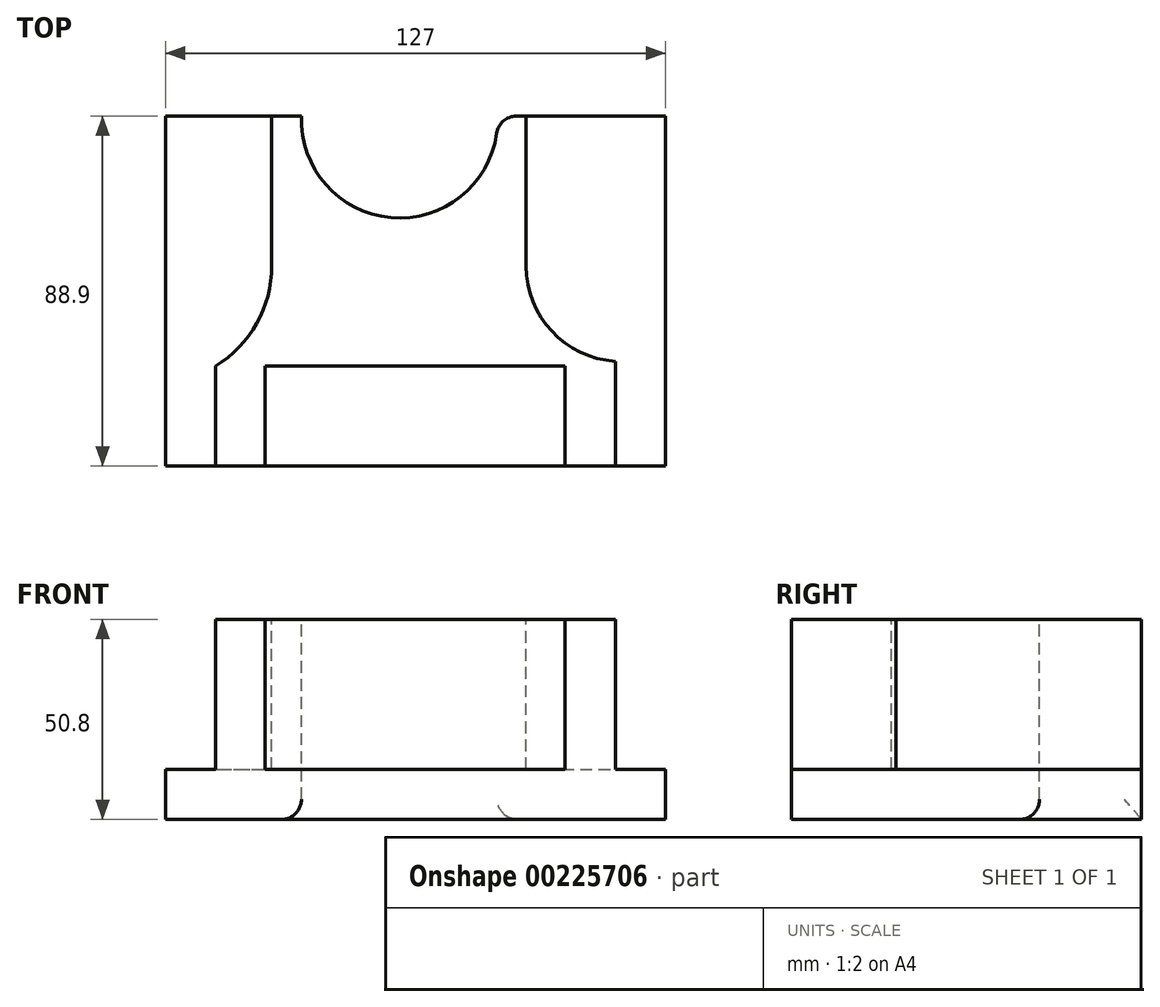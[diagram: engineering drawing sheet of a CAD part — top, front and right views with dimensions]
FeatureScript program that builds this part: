
annotation { "Feature Type Name" : "Feature", "Feature Type Description" : "" }
export const myFeature = defineFeature(function(context is Context, id is Id, definition is map)
    precondition{}
    {
        {
            var Q0;
            Q0=qCreatedBy(makeId("Top.planeOp"),FACE);
            var sketch = newSketch(context, id + "F0", { "sketchPlane" : qUnion([Q0])});
            skLineSegment(sketch, "E0.bottom", {"start": v(-62.55, 34.48) * mm, "end": v(64.45, 34.48) * mm});
            skLineSegment(sketch, "E0.top", {"start": v(-62.55, -54.42) * mm, "end": v(64.45, -54.42) * mm});
            skLineSegment(sketch, "E0.left", {"start": v(-62.55, 34.48) * mm, "end": v(-62.55, -54.42) * mm});
            skLineSegment(sketch, "E0.right", {"start": v(64.45, 34.48) * mm, "end": v(64.45, -54.42) * mm});
            skSolve(sketch);
        }
        {
            var Q0;
            Q0=makeQuery(id+"F0.imprint","IMPRINT",FACE,{"disambiguationData":[TD([[makeQuery(id+"F0.imprint","IMPRINT",EDGE,{"derivedFrom":sQuery(id+"F0.wireOp",EDGE,"E0.bottom")}),-1.0]])]});
            extrude(context, id + "F1", {"entities" : qUnion([Q0]), "depth" : 50.8 * mm});
        }
        {
            var Q0;
            Q0=makeQuery(id+"F1.opExtrude","CAP_FACE",FACE,{"disambiguationData":[OSD([sQuery(id+"F0.wireOp",EDGE,"E0.bottom"),sQuery(id+"F0.wireOp",EDGE,"E0.top"),sQuery(id+"F0.wireOp",EDGE,"E0.left"),sQuery(id+"F0.wireOp",EDGE,"E0.right")])],"isStart":false});
            var sketch = newSketch(context, id + "F2", { "sketchPlane" : qUnion([Q0])});
            skArc(sketch, "E1", {"start": v(-28.02, 34.48) * mm, "mid": v(-3.13, 8.61) * mm, "end": v(21.76, 34.48) * mm});
            skSolve(sketch);
        }
        {
            var Q0;
            {var subQ0=sQuery(id+"F2.wireOp",EDGE,"E1");Q0=makeQuery(id+"F2.imprint","IMPRINT",FACE,{"disambiguationData":[TD([[makeQuery(id+"F2.imprint","IMPRINT",EDGE,{"derivedFrom":subQ0}),1.0]])]});}
            extrude(context, id + "F3", {"entities" : qUnion([Q0]), "operationType" : NewBodyOperationType.REMOVE, "oppositeDirection" : true, "depth" : 76.2 * mm});
        }
        {
            var Q0;
            Q0=makeQuery(id+"F1.opExtrude","CAP_FACE",FACE,{"disambiguationData":[OSD([sQuery(id+"F0.wireOp",EDGE,"E0.bottom"),sQuery(id+"F0.wireOp",EDGE,"E0.top"),sQuery(id+"F0.wireOp",EDGE,"E0.left"),sQuery(id+"F0.wireOp",EDGE,"E0.right")])],"isStart":false});
            var sketch = newSketch(context, id + "F4", { "sketchPlane" : qUnion([Q0])});
            skLineSegment(sketch, "E2.bottom", {"start": v(-37.27, -54.42) * mm, "end": v(38.93, -54.42) * mm});
            skLineSegment(sketch, "E2.top", {"start": v(-37.27, -29.02) * mm, "end": v(38.93, -29.02) * mm});
            skLineSegment(sketch, "E2.left", {"start": v(-37.27, -54.42) * mm, "end": v(-37.27, -29.02) * mm});
            skLineSegment(sketch, "E2.right", {"start": v(38.93, -54.42) * mm, "end": v(38.93, -29.02) * mm});
            skSolve(sketch);
        }
        {
            var Q0;
            Q0=makeQuery(id+"F4.imprint","IMPRINT",FACE,{"disambiguationData":[TD([[makeQuery(id+"F4.imprint","IMPRINT",EDGE,{"derivedFrom":sQuery(id+"F4.wireOp",EDGE,"E2.bottom")}),1.0]])]});
            extrude(context, id + "F5", {"entities" : qUnion([Q0]), "operationType" : NewBodyOperationType.REMOVE, "oppositeDirection" : true, "depth" : 38.1 * mm});
        }
        {
            var Q0;
            Q0=makeQuery(id+"F1.opExtrude","CAP_FACE",FACE,{"disambiguationData":[OSD([sQuery(id+"F0.wireOp",EDGE,"E0.bottom"),sQuery(id+"F0.wireOp",EDGE,"E0.top"),sQuery(id+"F0.wireOp",EDGE,"E0.left"),sQuery(id+"F0.wireOp",EDGE,"E0.right")])],"isStart":false});
            var sketch = newSketch(context, id + "F6", { "sketchPlane" : qUnion([Q0])});
            skLineSegment(sketch, "E3", {"start": v(-49.9, -54.42) * mm, "end": v(-49.9, -29.02) * mm});
            skLineSegment(sketch, "E4", {"start": v(51.7, -54.42) * mm, "end": v(51.7, -27.82) * mm});
            skLineSegment(sketch, "E5", {"start": v(-35.57, 34.48) * mm, "end": v(-35.57, -3.62) * mm});
            skLineSegment(sketch, "E6", {"start": v(29.03, 34.48) * mm, "end": v(29.03, -3.62) * mm});
            skArc(sketch, "E7", {"start": v(-49.9, -29.02) * mm, "mid": v(-39.4, -18.2) * mm, "end": v(-35.57, -3.62) * mm});
            skArc(sketch, "E8", {"start": v(29.03, -3.62) * mm, "mid": v(35.58, -20.2) * mm, "end": v(51.7, -27.82) * mm});
            skSolve(sketch);
        }
        {
            var Q0;
            {var subQ7=sQuery(id+"F6.wireOp",EDGE,"E3");Q0=makeQuery(id+"F6.imprint","IMPRINT",FACE,{"disambiguationData":[TD([[makeQuery(id+"F6.imprint","IMPRINT",EDGE,{"derivedFrom":subQ7}),1.0]])]});}
            var Q1;
            {var subQ8=sQuery(id+"F6.wireOp",EDGE,"E4");Q1=makeQuery(id+"F6.imprint","IMPRINT",FACE,{"disambiguationData":[TD([[makeQuery(id+"F6.imprint","IMPRINT",EDGE,{"derivedFrom":subQ8}),-1.0]])]});}
            extrude(context, id + "F7", {"entities" : qUnion([Q0, Q1]), "operationType" : NewBodyOperationType.REMOVE, "oppositeDirection" : true, "depth" : 38.1 * mm});
        }
        {
            var Q0;
            Q0=makeQuery(id+"F5.boolean.opBoolean","COPY",EDGE,{"derivedFrom":makeQuery(id+"F5.opExtrude","CAP_EDGE",EDGE,{"disambiguationData":[OSD([sQuery(id+"F4.wireOp",EDGE,"E2.top")])],"isStart":true})});
            var Q1;
            Q1=makeQuery(id+"F5.boolean.opBoolean","COPY",EDGE,{"derivedFrom":makeQuery(id+"F5.opExtrude","CAP_EDGE",EDGE,{"disambiguationData":[OSD([sQuery(id+"F4.wireOp",EDGE,"E2.left")])],"isStart":true})});
            var Q2;
            Q2=makeQuery(id+"F5.boolean.opBoolean","COPY",EDGE,{"derivedFrom":makeQuery(id+"F5.opExtrude","CAP_EDGE",EDGE,{"disambiguationData":[OSD([sQuery(id+"F4.wireOp",EDGE,"E2.right")])],"isStart":true})});
            var Q3;
            Q3=makeQuery(id+"F5.boolean.opBoolean","COPY",EDGE,{"derivedFrom":makeQuery(id+"F5.opExtrude","CAP_EDGE",EDGE,{"disambiguationData":[OSD([sQuery(id+"F4.wireOp",EDGE,"E2.bottom")])],"isStart":false})});
            var Q4;
            Q4=makeQuery(id+"F3.boolean.opBoolean","COPY",EDGE,{"derivedFrom":makeQuery(id+"F3.opExtrude","CAP_EDGE",EDGE,{"disambiguationData":[OSD([sQuery(id+"F2.wireOp",EDGE,"E1")])],"isStart":true})});
            var Q5;
            {var subQ0=sQuery(id+"F2.wireOp",EDGE,"E1");var subQ1=sQuery(id+"F0.wireOp",EDGE,"E0.bottom");Q5=makeQuery(id+"F3.boolean.opBoolean","COPY",EDGE,{"derivedFrom":makeQuery(id+"F3.opExtrude","SWEPT_EDGE",EDGE,{"disambiguationData":[OSD([subQ1,subQ0]),TDD([makeQuery(id+"F2.imprint","INTERSECT",VERTEX,{"disambiguationData":[OD(1.0)],"derivedFrom":[makeQuery(id+"F1.opExtrude","CAP_EDGE",EDGE,{"disambiguationData":[OSD([subQ1])],"isStart":false}),subQ0]})])]})});}
            var Q6;
            {var subQ0=sQuery(id+"F2.wireOp",EDGE,"E1");var subQ1=sQuery(id+"F0.wireOp",EDGE,"E0.bottom");Q6=makeQuery(id+"F3.boolean.opBoolean","COPY",EDGE,{"derivedFrom":makeQuery(id+"F3.opExtrude","SWEPT_EDGE",EDGE,{"disambiguationData":[OSD([subQ1,subQ0]),TDD([makeQuery(id+"F2.imprint","INTERSECT",VERTEX,{"disambiguationData":[OD(0.0)],"derivedFrom":[makeQuery(id+"F1.opExtrude","CAP_EDGE",EDGE,{"disambiguationData":[OSD([subQ1])],"isStart":false}),subQ0]})])]})});}
            var Q7;
            Q7=makeQuery(id+"F3.boolean.opBoolean","INTERSECT",EDGE,{"derivedFrom":[makeQuery(id+"F1.opExtrude","CAP_FACE",FACE,{"disambiguationData":[OSD([sQuery(id+"F0.wireOp",EDGE,"E0.bottom"),sQuery(id+"F0.wireOp",EDGE,"E0.top"),sQuery(id+"F0.wireOp",EDGE,"E0.left"),sQuery(id+"F0.wireOp",EDGE,"E0.right")])],"isStart":true}),makeQuery(id+"F3.opExtrude","SWEPT_FACE",FACE,{"disambiguationData":[OSD([sQuery(id+"F2.wireOp",EDGE,"E1")])]})]});
            fillet(context, id + "F8", {"entities" : qUnion([Q0, Q1, Q2, Q3, Q4, Q5, Q6, Q7]), "radius" : 5.08 * mm, "tangentPropagation" : true, "allowEdgeOverflow" : false});
        }
    });
